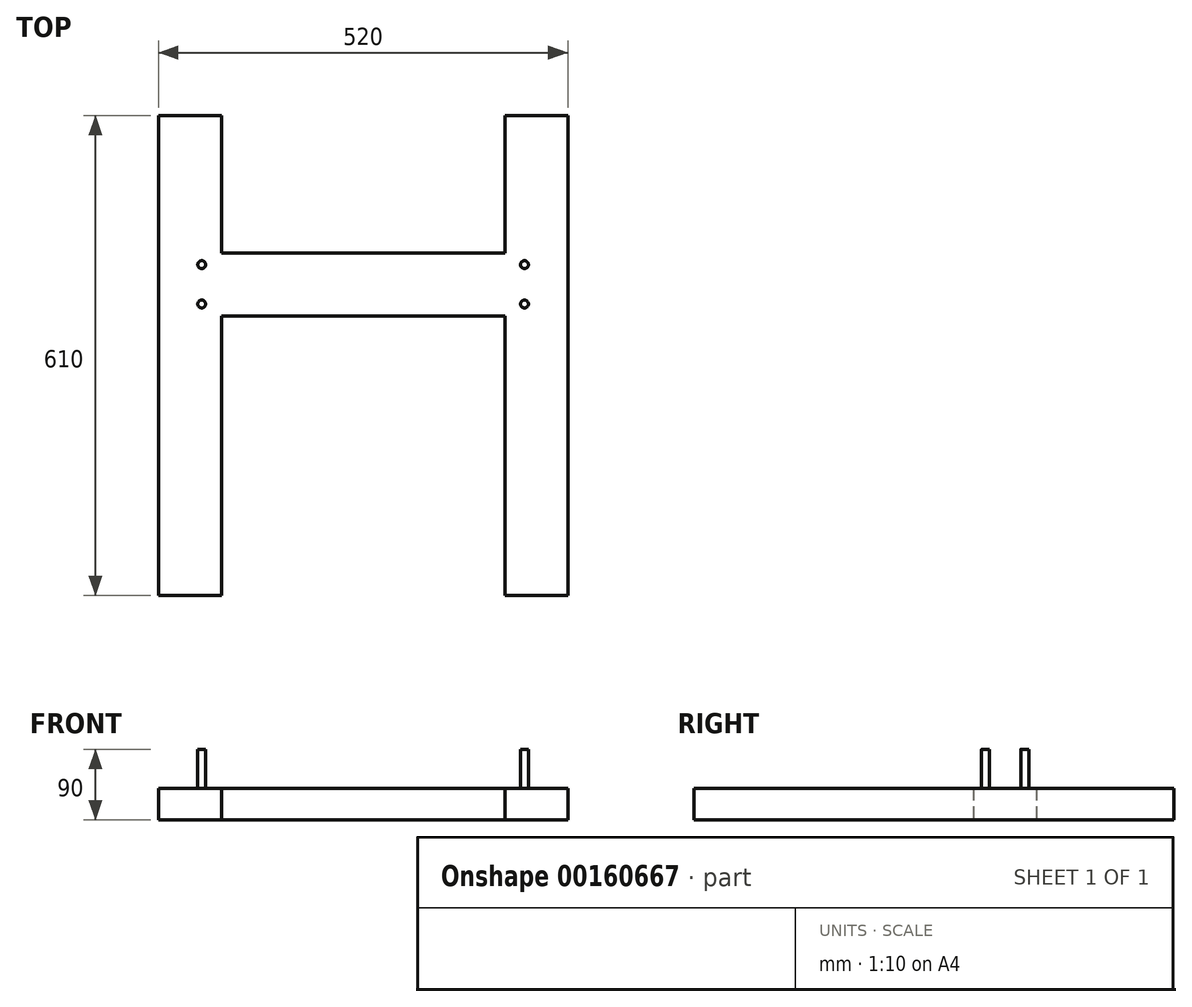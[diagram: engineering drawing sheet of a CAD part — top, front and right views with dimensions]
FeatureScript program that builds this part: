
annotation { "Feature Type Name" : "Feature", "Feature Type Description" : "" }
export const myFeature = defineFeature(function(context is Context, id is Id, definition is map)
    precondition{}
    {
        {
            var Q0;
            Q0=qCreatedBy(makeId("Top.planeOp"),FACE);
            var sketch = newSketch(context, id + "F0", { "sketchPlane" : qUnion([Q0])});
            skLineSegment(sketch, "E0.bottom", {"start": v(-260, 214.5) * mm, "end": v(-180, 214.5) * mm});
            skLineSegment(sketch, "E0.top", {"start": v(-260, -395.5) * mm, "end": v(-180, -395.5) * mm});
            skLineSegment(sketch, "E0.left", {"start": v(-260, 214.5) * mm, "end": v(-260, -395.5) * mm});
            skLineSegment(sketch, "E0.right", {"start": v(-180, 214.5) * mm, "end": v(-180, 40) * mm});
            skLineSegment(sketch, "E1.bottom", {"start": v(180, 214.5) * mm, "end": v(260, 214.5) * mm});
            skLineSegment(sketch, "E1.top", {"start": v(180, -395.5) * mm, "end": v(260, -395.5) * mm});
            skLineSegment(sketch, "E1.left", {"start": v(180, 214.5) * mm, "end": v(180, 40) * mm});
            skLineSegment(sketch, "E1.right", {"start": v(260, 214.5) * mm, "end": v(260, -395.5) * mm});
            skLineSegment(sketch, "E2.bottom", {"start": v(-180, 40) * mm, "end": v(180, 40) * mm});
            skLineSegment(sketch, "E2.top", {"start": v(-180, -40) * mm, "end": v(180, -40) * mm});
            skLineSegment(sketch, "E3.trimOffspring", {"start": v(-180, -40) * mm, "end": v(-180, -395.5) * mm});
            skLineSegment(sketch, "E4.trimOffspring", {"start": v(180, -40) * mm, "end": v(180, -395.5) * mm});
            skSolve(sketch);
        }
        {
            var Q0;
            Q0=makeQuery(id+"F0.imprint","IMPRINT",FACE,{"disambiguationData":[TD([[makeQuery(id+"F0.imprint","IMPRINT",EDGE,{"derivedFrom":sQuery(id+"F0.wireOp",EDGE,"E0.bottom")}),-1.0]])]});
            extrude(context, id + "F1", {"entities" : qUnion([Q0]), "depth" : 40 * mm});
        }
        {
            var Q0;
            Q0=makeQuery(id+"F1.opExtrude","CAP_FACE",FACE,{"disambiguationData":[OSD([sQuery(id+"F0.wireOp",EDGE,"E0.bottom"),sQuery(id+"F0.wireOp",EDGE,"E0.top"),sQuery(id+"F0.wireOp",EDGE,"E0.left"),sQuery(id+"F0.wireOp",EDGE,"E0.right"),sQuery(id+"F0.wireOp",EDGE,"E1.bottom"),sQuery(id+"F0.wireOp",EDGE,"E1.top"),sQuery(id+"F0.wireOp",EDGE,"E1.left"),sQuery(id+"F0.wireOp",EDGE,"E1.right"),sQuery(id+"F0.wireOp",EDGE,"E2.bottom"),sQuery(id+"F0.wireOp",EDGE,"E2.top"),sQuery(id+"F0.wireOp",EDGE,"E3.trimOffspring"),sQuery(id+"F0.wireOp",EDGE,"E4.trimOffspring")])],"isStart":false});
            var sketch = newSketch(context, id + "F2", { "sketchPlane" : qUnion([Q0])});
            skCircle(sketch, "E5", {"center": v(-205, 25) * mm, "radius": 5 * mm});
            skCircle(sketch, "E6", {"center": v(-205, -25) * mm, "radius": 5 * mm});
            skCircle(sketch, "E7.MirrorC", {"center": v(205, 25) * mm, "radius": 5 * mm});
            skCircle(sketch, "E8.MirrorC", {"center": v(205, -25) * mm, "radius": 5 * mm});
            skSolve(sketch);
        }
        {
            var Q0;
            Q0 = qSketchRegion(id + "F2", true);
            extrude(context, id + "F3", {"entities" : qUnion([Q0]), "operationType" : NewBodyOperationType.ADD, "depth" : 50 * mm});
        }
    });
